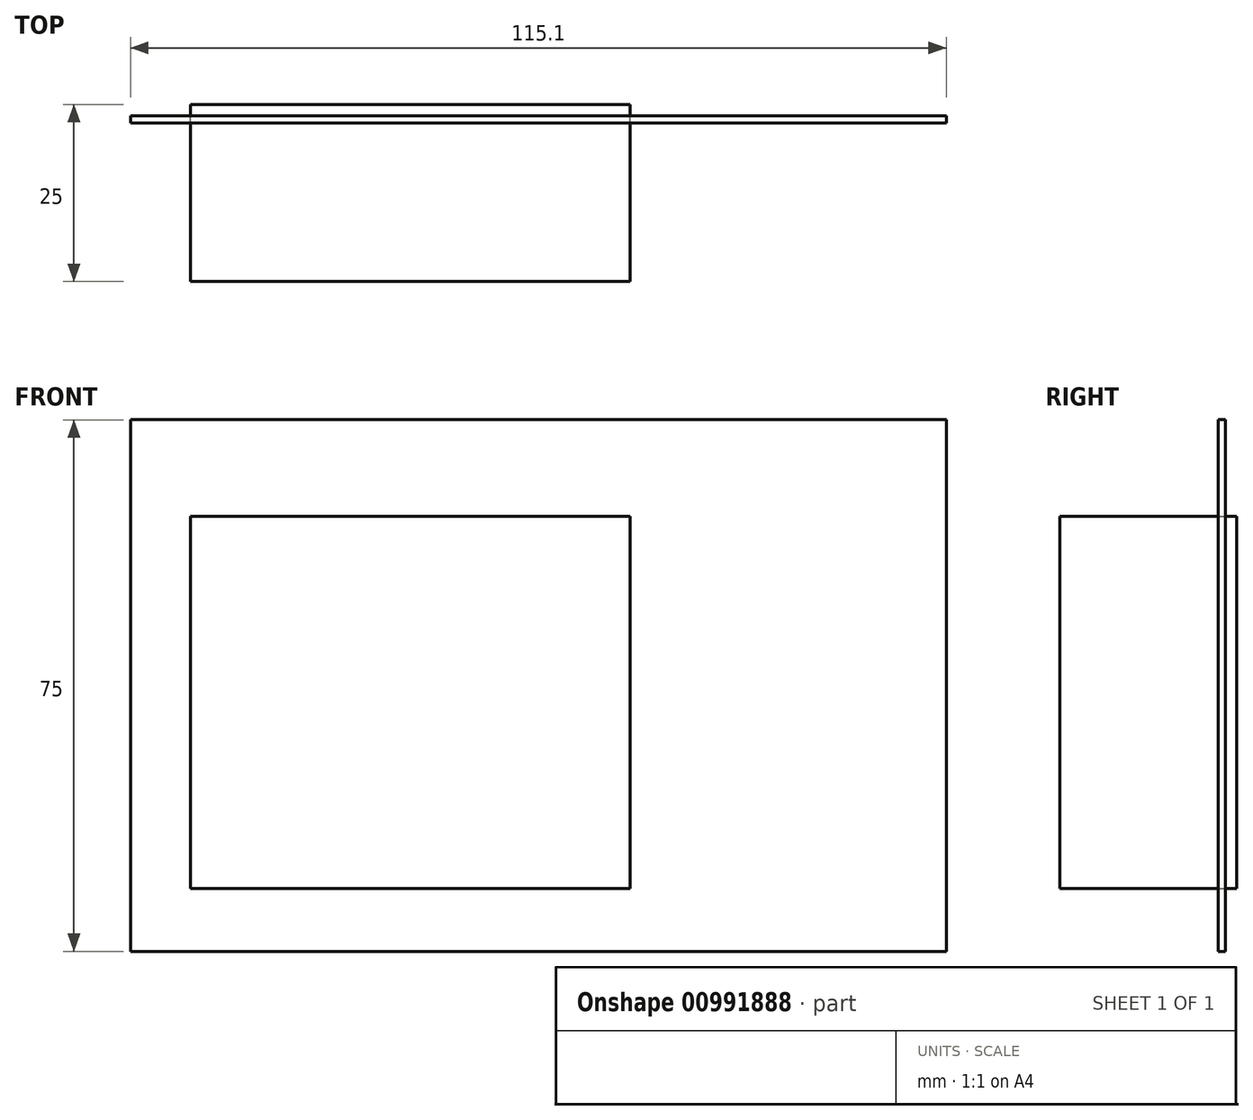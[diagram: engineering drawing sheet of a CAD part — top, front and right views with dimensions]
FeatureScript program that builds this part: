
annotation { "Feature Type Name" : "Feature", "Feature Type Description" : "" }
export const myFeature = defineFeature(function(context is Context, id is Id, definition is map)
    precondition{}
    {
        {
            var Q0;
            Q0=qCreatedBy(makeId("Front.planeOp"),FACE);
            var sketch = newSketch(context, id + "F0", { "sketchPlane" : qUnion([Q0])});
            skLineSegment(sketch, "E0.bottom", {"start": v(26.1, 10.25) * mm, "end": v(-89, 10.25) * mm});
            skLineSegment(sketch, "E0.top", {"start": v(26.1, 85.25) * mm, "end": v(-89, 85.25) * mm});
            skLineSegment(sketch, "E0.left", {"start": v(26.1, 10.25) * mm, "end": v(26.1, 85.25) * mm});
            skLineSegment(sketch, "E0.right", {"start": v(-89, 10.25) * mm, "end": v(-89, 85.25) * mm});
            skPoint(sketch, "E0.middle", {"position": v(-31.45, 47.75) * mm});
            skSolve(sketch);
        }
        {
            var Q0;
            Q0=makeQuery(id+"F0.imprint","IMPRINT",FACE,{"disambiguationData":[TD([[makeQuery(id+"F0.imprint","IMPRINT",EDGE,{"derivedFrom":sQuery(id+"F0.wireOp",EDGE,"E0.bottom")}),-1.0]])]});
            extrude(context, id + "F1", {"entities" : qUnion([Q0]), "depth" : 1 * mm, "offsetDistance" : 25 * mm});
        }
        {
            var Q0;
            Q0=qCreatedBy(makeId("Front.planeOp"),FACE);
            var sketch = newSketch(context, id + "F2", { "sketchPlane" : qUnion([Q0])});
            skLineSegment(sketch, "E1.bottom", {"start": v(6.07, -42.28) * mm, "end": v(-55.93, -42.28) * mm});
            skLineSegment(sketch, "E1.top", {"start": v(6.07, 10.22) * mm, "end": v(-55.93, 10.22) * mm});
            skLineSegment(sketch, "E1.left", {"start": v(6.07, -42.28) * mm, "end": v(6.07, 10.22) * mm});
            skLineSegment(sketch, "E1.right", {"start": v(-55.93, -42.28) * mm, "end": v(-55.93, 10.22) * mm});
            skPoint(sketch, "E1.middle", {"position": v(-24.93, -16.03) * mm});
            skSolve(sketch);
        }
        {
            var Q0;
            Q0=makeQuery(id+"F2.imprint","IMPRINT",FACE,{"disambiguationData":[TD([[makeQuery(id+"F2.imprint","IMPRINT",EDGE,{"derivedFrom":sQuery(id+"F2.wireOp",EDGE,"E1.bottom")}),-1.0]])]});
            extrude(context, id + "F3", {"entities" : qUnion([Q0]), "depth" : 25 * mm, "offsetDistance" : 25 * mm});
        }
        {
            var Q0;
            Q0=makeQuery(id+"F3.opExtrude","SWEPT_BODY",BODY,{"disambiguationData":[OSD([sQuery(id+"F2.wireOp",EDGE,"E1.bottom"),sQuery(id+"F2.wireOp",EDGE,"E1.top"),sQuery(id+"F2.wireOp",EDGE,"E1.left"),sQuery(id+"F2.wireOp",EDGE,"E1.right")])]});
            transform(context, id + "F4", {"entities" : qUnion([Q0]), "transformType" : TransformType.TRANSLATION_3D, "dx" : -24.6 * mm, "dy" : 0 * mm, "dz" : 61.4 * mm, "makeCopy" : false});
        }
        {
            var Q0;
            Q0=makeQuery(id+"F3.opExtrude","SWEPT_BODY",BODY,{"disambiguationData":[OSD([sQuery(id+"F2.wireOp",EDGE,"E1.bottom"),sQuery(id+"F2.wireOp",EDGE,"E1.top"),sQuery(id+"F2.wireOp",EDGE,"E1.left"),sQuery(id+"F2.wireOp",EDGE,"E1.right")])]});
            transform(context, id + "F5", {"entities" : qUnion([Q0]), "transformType" : TransformType.TRANSLATION_3D, "dx" : 0 * mm, "dy" : 1.6 * mm, "dz" : 0 * mm, "makeCopy" : false});
        }
    });
